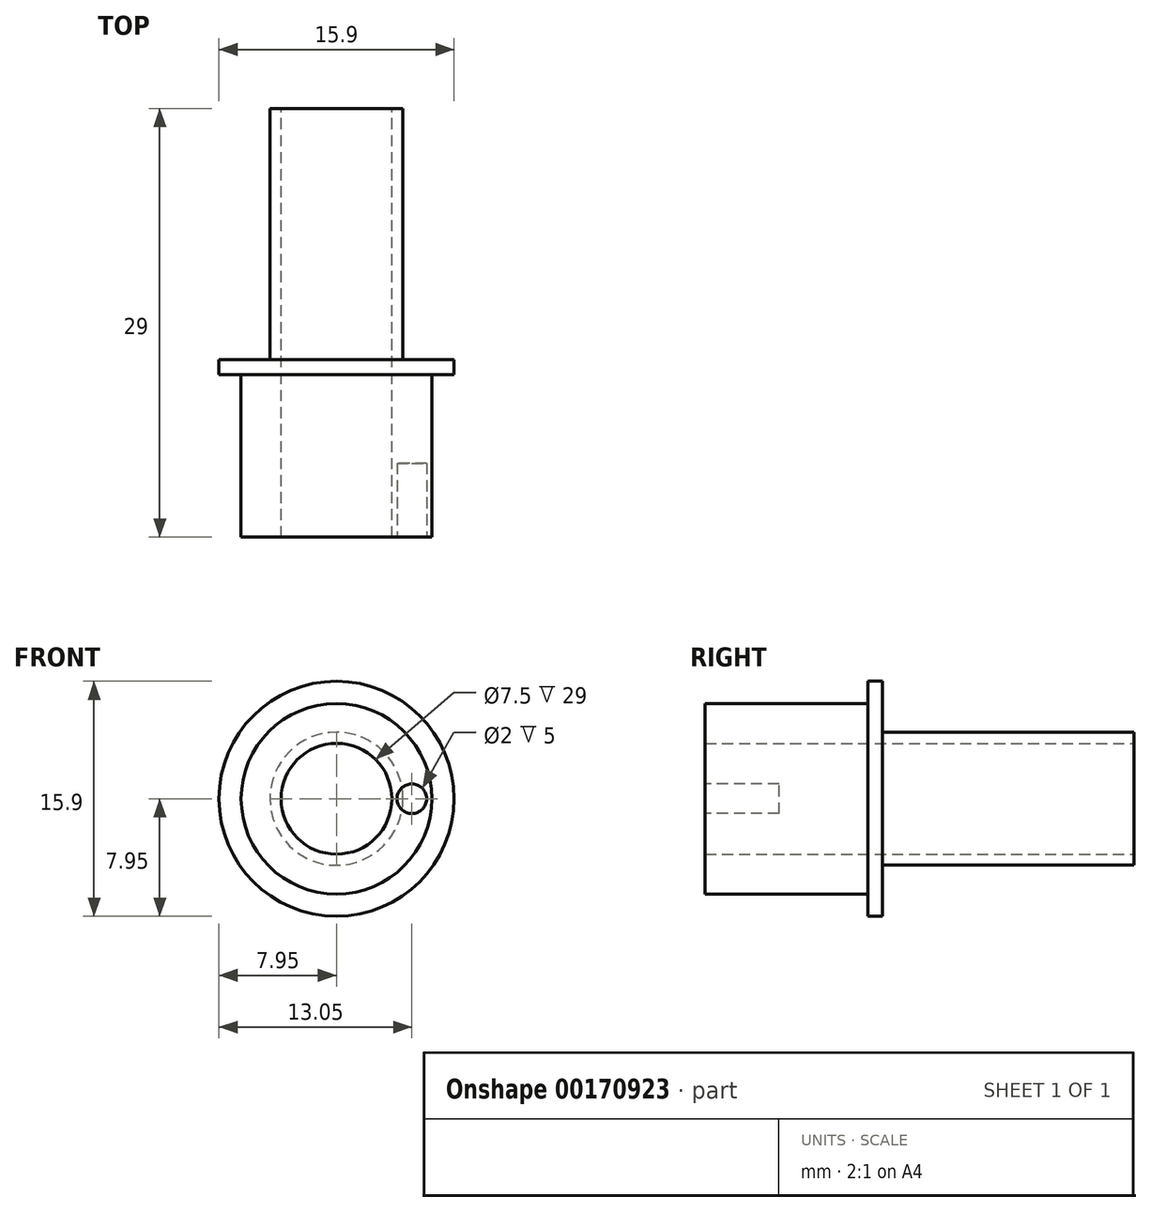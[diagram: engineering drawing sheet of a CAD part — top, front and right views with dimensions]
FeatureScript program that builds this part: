
annotation { "Feature Type Name" : "Feature", "Feature Type Description" : "" }
export const myFeature = defineFeature(function(context is Context, id is Id, definition is map)
    precondition{}
    {
        {
            var Q0;
            Q0=qCreatedBy(makeId("Right.planeOp"),FACE);
            var sketch = newSketch(context, id + "F0", { "sketchPlane" : qUnion([Q0])});
            skLineSegment(sketch, "E0", {"start": v(29, 0) * mm, "end": v(0, 0) * mm, "construction": true});
            skLineSegment(sketch, "E1", {"start": v(29, 3.75) * mm, "end": v(0, 3.75) * mm});
            skLineSegment(sketch, "E2", {"start": v(0, 6.45) * mm, "end": v(0, 3.75) * mm});
            skLineSegment(sketch, "E3", {"start": v(11, 6.45) * mm, "end": v(11, 7.95) * mm});
            skLineSegment(sketch, "E4", {"start": v(11, 7.95) * mm, "end": v(12, 7.95) * mm});
            skLineSegment(sketch, "E5", {"start": v(12, 7.95) * mm, "end": v(12, 4.5) * mm});
            skLineSegment(sketch, "E6.trimOffspring", {"start": v(11, 6.45) * mm, "end": v(0, 6.45) * mm});
            skLineSegment(sketch, "E7", {"start": v(12, 4.5) * mm, "end": v(29, 4.5) * mm});
            skLineSegment(sketch, "E8", {"start": v(29, 4.5) * mm, "end": v(29, 3.75) * mm});
            skSolve(sketch);
        }
        {
            var Q0;
            Q0=makeQuery(id+"F0.imprint","IMPRINT",FACE,{"disambiguationData":[TD([[makeQuery(id+"F0.imprint","IMPRINT",EDGE,{"derivedFrom":sQuery(id+"F0.wireOp",EDGE,"E1")}),-1.0]])]});
            var Q1;
            Q1=sQuery(id+"F0.wireOp",EDGE,"E0");
            revolve(context, id + "F1", {"entities" : qUnion([Q0]), "axis" : qUnion([Q1]), "revolveType" : RevolveType.FULL});
        }
        {
            var Q0;
            Q0=makeQuery(id+"F1.opRevolve","SWEPT_FACE",FACE,{"disambiguationData":[OSD([sQuery(id+"F0.wireOp",EDGE,"E2")])]});
            var sketch = newSketch(context, id + "F2", { "sketchPlane" : qUnion([Q0])});
            skCircle(sketch, "E9", {"center": v(0, 0) * mm, "radius": 5.1 * mm, "construction": true});
            skCircle(sketch, "E10", {"center": v(5.1, 0) * mm, "radius": 1 * mm});
            skSolve(sketch);
        }
        {
            var Q0;
            Q0=makeQuery(id+"F2.imprint","IMPRINT",FACE,{"disambiguationData":[TD([[makeQuery(id+"F2.imprint","IMPRINT",EDGE,{"derivedFrom":sQuery(id+"F2.wireOp",EDGE,"E10")}),1.0]])]});
            extrude(context, id + "F3", {"entities" : qUnion([Q0]), "operationType" : NewBodyOperationType.REMOVE, "oppositeDirection" : true, "depth" : 5 * mm});
        }
    });
